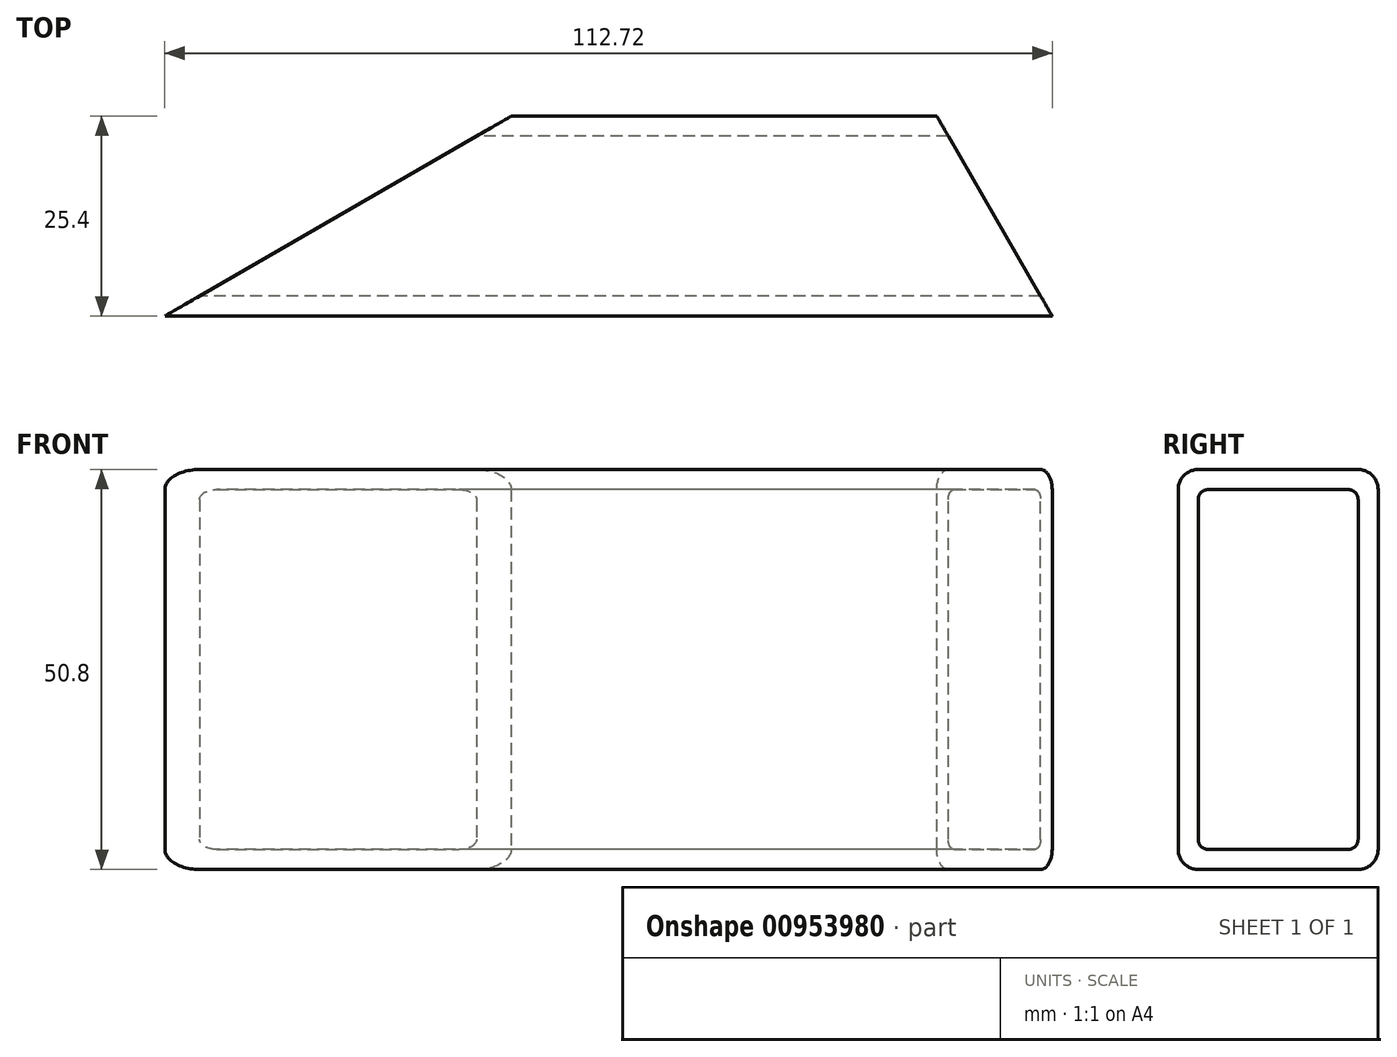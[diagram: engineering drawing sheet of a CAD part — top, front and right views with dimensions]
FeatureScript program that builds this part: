
annotation { "Feature Type Name" : "Feature", "Feature Type Description" : "" }
export const myFeature = defineFeature(function(context is Context, id is Id, definition is map)
    precondition{}
    {
        {
            var Q0;
            Q0=qCreatedBy(makeId("Front.planeOp"),FACE);
            var sketch = newSketch(context, id + "F0", { "sketchPlane" : qUnion([Q0])});
            skLineSegment(sketch, "E0.bottom", {"start": v(56.36, -25.4) * mm, "end": v(-56.36, -25.4) * mm});
            skLineSegment(sketch, "E0.top", {"start": v(56.36, 25.4) * mm, "end": v(-56.36, 25.4) * mm});
            skLineSegment(sketch, "E0.left", {"start": v(56.36, -25.4) * mm, "end": v(56.36, 25.4) * mm});
            skLineSegment(sketch, "E0.right", {"start": v(-56.36, -25.4) * mm, "end": v(-56.36, 25.4) * mm});
            skPoint(sketch, "E0.middle", {"position": v(0, 0) * mm});
            skSolve(sketch);
        }
        {
            var Q0;
            Q0=makeQuery(id+"F0.imprint","IMPRINT",FACE,{"disambiguationData":[TD([[makeQuery(id+"F0.imprint","IMPRINT",EDGE,{"derivedFrom":sQuery(id+"F0.wireOp",EDGE,"E0.bottom")}),-1.0]])]});
            extrude(context, id + "F1", {"entities" : qUnion([Q0]), "endBound" : BoundingType.SYMMETRIC, "depth" : 25.4 * mm, "offsetDistance" : 25.4 * mm});
        }
        {
            var Q0;
            Q0=makeQuery(id+"F1.opExtrude","SWEPT_FACE",FACE,{"disambiguationData":[OSD([sQuery(id+"F0.wireOp",EDGE,"E0.right")])]});
            var Q1;
            Q1=makeQuery(id+"F1.opExtrude","SWEPT_FACE",FACE,{"disambiguationData":[OSD([sQuery(id+"F0.wireOp",EDGE,"E0.left")])]});
            shell(context, id + "F2", {"entities" : qUnion([Q0, Q1]), "thickness" : 2.54 * mm});
        }
        {
            var Q0;
            Q0=makeQuery(id+"F1.opExtrude","SWEPT_FACE",FACE,{"disambiguationData":[OSD([sQuery(id+"F0.wireOp",EDGE,"E0.bottom")])]});
            var sketch = newSketch(context, id + "F3", { "sketchPlane" : qUnion([Q0])});
            skLineSegment(sketch, "E1", {"start": v(-56.36, 12.7) * mm, "end": v(-12.36, -12.7) * mm});
            skLineSegment(sketch, "E2", {"start": v(-12.36, -12.7) * mm, "end": v(-56.36, -12.7) * mm});
            skLineSegment(sketch, "E3", {"start": v(-56.36, -12.7) * mm, "end": v(-56.36, 12.7) * mm});
            skSolve(sketch);
        }
        {
            var Q0;
            Q0 = qSketchRegion(id + "F3", true);
            extrude(context, id + "F4", {"entities" : qUnion([Q0]), "operationType" : NewBodyOperationType.REMOVE, "endBound" : BoundingType.THROUGH_ALL, "oppositeDirection" : true, "depth" : 25.4 * mm, "offsetDistance" : 25.4 * mm});
        }
        {
            var Q0;
            Q0=makeQuery(id+"F1.opExtrude","SWEPT_FACE",FACE,{"disambiguationData":[OSD([sQuery(id+"F0.wireOp",EDGE,"E0.top")])]});
            var sketch = newSketch(context, id + "F5", { "sketchPlane" : qUnion([Q0])});
            skLineSegment(sketch, "E4", {"start": v(56.36, -12.7) * mm, "end": v(41.7, 12.7) * mm});
            skLineSegment(sketch, "E5", {"start": v(41.7, 12.7) * mm, "end": v(56.36, 12.7) * mm});
            skLineSegment(sketch, "E6", {"start": v(56.36, 12.7) * mm, "end": v(56.36, -12.7) * mm});
            skSolve(sketch);
        }
        {
            var Q0;
            Q0=makeQuery(id+"F5.imprint","IMPRINT",FACE,{"disambiguationData":[TD([[makeQuery(id+"F5.imprint","IMPRINT",EDGE,{"derivedFrom":sQuery(id+"F5.wireOp",EDGE,"E4")}),-1.0]])]});
            extrude(context, id + "F6", {"entities" : qUnion([Q0]), "operationType" : NewBodyOperationType.REMOVE, "endBound" : BoundingType.THROUGH_ALL, "oppositeDirection" : true, "depth" : 25.4 * mm, "offsetDistance" : 25.4 * mm});
        }
        {
            var Q0;
            Q0=makeQuery(id+"F1.opExtrude","CAP_EDGE",EDGE,{"disambiguationData":[OSD([sQuery(id+"F0.wireOp",EDGE,"E0.top")])],"isStart":false});
            var Q1;
            Q1=makeQuery(id+"F1.opExtrude","CAP_EDGE",EDGE,{"disambiguationData":[OSD([sQuery(id+"F0.wireOp",EDGE,"E0.top")])],"isStart":true});
            var Q2;
            Q2=makeQuery(id+"F1.opExtrude","CAP_EDGE",EDGE,{"disambiguationData":[OSD([sQuery(id+"F0.wireOp",EDGE,"E0.bottom")])],"isStart":true});
            var Q3;
            Q3=makeQuery(id+"F1.opExtrude","CAP_EDGE",EDGE,{"disambiguationData":[OSD([sQuery(id+"F0.wireOp",EDGE,"E0.bottom")])],"isStart":false});
            fillet(context, id + "F7", {"entities" : qUnion([Q0, Q1, Q2, Q3]), "radius" : 2.54 * mm, "tangentPropagation" : true, "allowEdgeOverflow" : false});
        }
        {
            var Q0;
            {var subQ0=sQuery(id+"F0.wireOp",EDGE,"E0.top");Q0=makeQuery(id+"F2.opShell","OFFSET_EDGE",EDGE,{"disambiguationData":[OSD([subQ0]),TDD([makeQuery(id+"F1.opExtrude","CAP_EDGE",EDGE,{"disambiguationData":[OSD([subQ0])],"isStart":true})])]});}
            var Q1;
            {var subQ0=sQuery(id+"F0.wireOp",EDGE,"E0.top");Q1=makeQuery(id+"F2.opShell","OFFSET_EDGE",EDGE,{"disambiguationData":[OSD([subQ0]),TDD([makeQuery(id+"F1.opExtrude","CAP_EDGE",EDGE,{"disambiguationData":[OSD([subQ0])],"isStart":false})])]});}
            var Q2;
            {var subQ0=sQuery(id+"F0.wireOp",EDGE,"E0.bottom");Q2=makeQuery(id+"F2.opShell","OFFSET_EDGE",EDGE,{"disambiguationData":[OSD([subQ0]),TDD([makeQuery(id+"F1.opExtrude","CAP_EDGE",EDGE,{"disambiguationData":[OSD([subQ0])],"isStart":false})])]});}
            var Q3;
            {var subQ0=sQuery(id+"F0.wireOp",EDGE,"E0.bottom");Q3=makeQuery(id+"F2.opShell","OFFSET_EDGE",EDGE,{"disambiguationData":[OSD([subQ0]),TDD([makeQuery(id+"F1.opExtrude","CAP_EDGE",EDGE,{"disambiguationData":[OSD([subQ0])],"isStart":true})])]});}
            fillet(context, id + "F8", {"entities" : qUnion([Q0, Q1, Q2, Q3]), "radius" : 1.27 * mm, "tangentPropagation" : true, "allowEdgeOverflow" : false});
        }
    });
